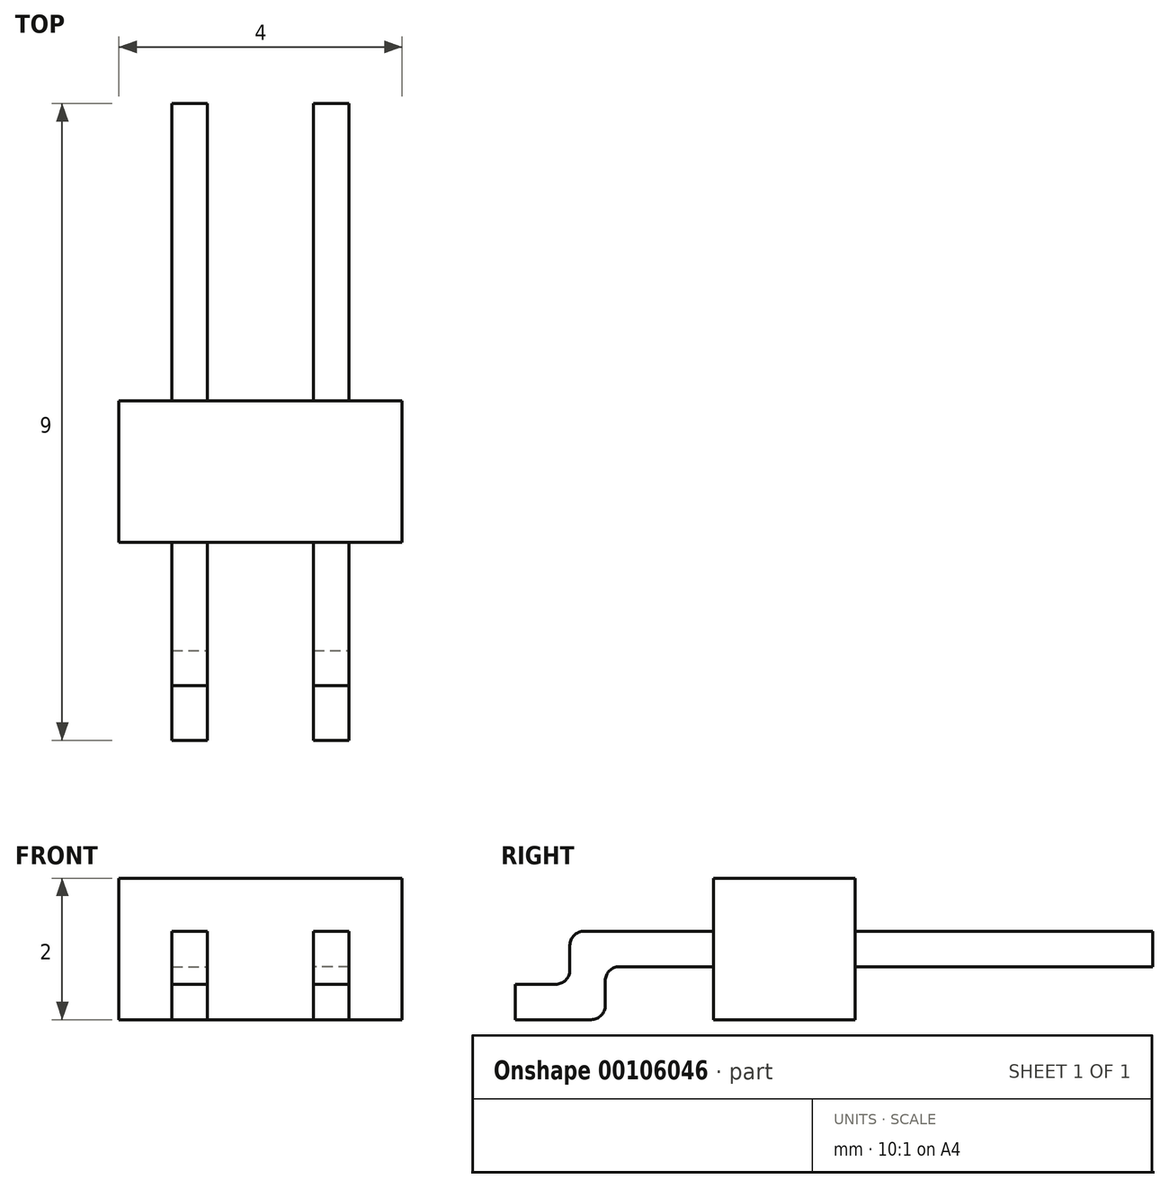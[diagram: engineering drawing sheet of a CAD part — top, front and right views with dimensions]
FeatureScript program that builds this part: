
annotation { "Feature Type Name" : "Feature", "Feature Type Description" : "" }
export const myFeature = defineFeature(function(context is Context, id is Id, definition is map)
    precondition{}
    {
        {
            var Q0;
            Q0=qCreatedBy(makeId("Top.planeOp"),FACE);
            var sketch = newSketch(context, id + "F0", { "sketchPlane" : qUnion([Q0])});
            skLineSegment(sketch, "E0.bottom", {"start": v(-2, 1) * mm, "end": v(2, 1) * mm});
            skLineSegment(sketch, "E0.top", {"start": v(-2, -1) * mm, "end": v(2, -1) * mm});
            skLineSegment(sketch, "E0.left", {"start": v(-2, 1) * mm, "end": v(-2, -1) * mm});
            skLineSegment(sketch, "E0.right", {"start": v(2, 1) * mm, "end": v(2, -1) * mm});
            skSolve(sketch);
        }
        {
            var Q0;
            Q0 = qSketchRegion(id + "F0", true);
            extrude(context, id + "F1", {"entities" : qUnion([Q0]), "depth" : 2 * mm});
        }
        {
            var Q0;
            Q0=makeQuery(id+"F1.opExtrude","SWEPT_FACE",FACE,{"disambiguationData":[OSD([sQuery(id+"F0.wireOp",EDGE,"E0.bottom")])]});
            var sketch = newSketch(context, id + "F2", { "sketchPlane" : qUnion([Q0])});
            skLineSegment(sketch, "E1.bottom", {"start": v(-1.25, 1.25) * mm, "end": v(-0.75, 1.25) * mm});
            skLineSegment(sketch, "E1.top", {"start": v(-1.25, 0.75) * mm, "end": v(-0.75, 0.75) * mm});
            skLineSegment(sketch, "E1.left", {"start": v(-1.25, 1.25) * mm, "end": v(-1.25, 0.75) * mm});
            skLineSegment(sketch, "E1.right", {"start": v(-0.75, 1.25) * mm, "end": v(-0.75, 0.75) * mm});
            skLineSegment(sketch, "E2.MirrorCS", {"start": v(0.75, 1.25) * mm, "end": v(0.75, 0.75) * mm});
            skLineSegment(sketch, "E3.MirrorCS", {"start": v(1.25, 1.25) * mm, "end": v(1.25, 0.75) * mm});
            skLineSegment(sketch, "E4.MirrorCS", {"start": v(1.25, 1.25) * mm, "end": v(0.75, 1.25) * mm});
            skLineSegment(sketch, "E5.MirrorCS", {"start": v(1.25, 0.75) * mm, "end": v(0.75, 0.75) * mm});
            skSolve(sketch);
        }
        {
            var Q0;
            Q0 = qSketchRegion(id + "F2", true);
            extrude(context, id + "F3", {"entities" : qUnion([Q0]), "depth" : 4.2 * mm});
        }
        {
            var Q0;
            Q0=makeQuery(id+"F3.opExtrude","SWEPT_FACE",FACE,{"disambiguationData":[OSD([sQuery(id+"F2.wireOp",EDGE,"E1.left")])]});
            var sketch = newSketch(context, id + "F4", { "sketchPlane" : qUnion([Q0])});
            skLineSegment(sketch, "E6.top", {"start": v(-1, 0.75) * mm, "end": v(-2.33, 0.75) * mm});
            skLineSegment(sketch, "E6.left", {"start": v(-1, 1.25) * mm, "end": v(-1, 0.75) * mm});
            skLineSegment(sketch, "E7.bottom", {"start": v(-3.8, 0) * mm, "end": v(-2.73, 0) * mm});
            skLineSegment(sketch, "E7.top", {"start": v(-3.8, 0.5) * mm, "end": v(-3.23, 0.5) * mm});
            skLineSegment(sketch, "E7.left", {"start": v(-3.8, 0) * mm, "end": v(-3.8, 0.5) * mm});
            skLineSegment(sketch, "E7.right", {"start": v(-2.53, 0.2) * mm, "end": v(-2.53, 0.6) * mm});
            skPoint(sketch, "E8.visualSharp", {"position": v(-2.53, 0) * mm});
            skArc(sketch, "E8.filletArc", {"start": v(-2.73, 0) * mm, "mid": v(-2.59, 0.06) * mm, "end": v(-2.53, 0.2) * mm});
            skLineSegment(sketch, "E9.bottom", {"start": v(-2.53, 0.2) * mm, "end": v(-3.13, 0.2) * mm});
            skLineSegment(sketch, "E9.top", {"start": v(-2.53, 1.25) * mm, "end": v(-2.83, 1.25) * mm});
            skLineSegment(sketch, "E9.left", {"start": v(-2.53, 0.2) * mm, "end": v(-2.53, 0.55) * mm});
            skLineSegment(sketch, "E9.right", {"start": v(-3.03, 0.7) * mm, "end": v(-3.03, 1.05) * mm});
            skArc(sketch, "E10.filletArc", {"start": v(-3.23, 0.5) * mm, "mid": v(-3.09, 0.56) * mm, "end": v(-3.03, 0.7) * mm});
            skPoint(sketch, "E11.visualSharp", {"position": v(-3.03, 1.25) * mm});
            skArc(sketch, "E11.filletArc", {"start": v(-2.83, 1.25) * mm, "mid": v(-2.97, 1.2) * mm, "end": v(-3.03, 1.05) * mm});
            skPoint(sketch, "E12.newPointA", {"position": v(-3.8, 0.75) * mm});
            skArc(sketch, "E12.filletArc", {"start": v(-2.33, 0.75) * mm, "mid": v(-2.47, 0.7) * mm, "end": v(-2.53, 0.55) * mm});
            skLineSegment(sketch, "E13", {"start": v(-2.53, 1.25) * mm, "end": v(-1, 1.25) * mm});
            skSolve(sketch);
        }
        {
            var Q0;
            Q0 = qSketchRegion(id + "F4", true);
            extrude(context, id + "F5", {"entities" : qUnion([Q0]), "oppositeDirection" : true, "depth" : 2.5 * mm});
        }
        {
            var Q0;
            Q0=makeQuery(id+"F5.opExtrude","SWEPT_FACE",FACE,{"disambiguationData":[OSD([sQuery(id+"F4.wireOp",EDGE,"E7.left")])]});
            var sketch = newSketch(context, id + "F6", { "sketchPlane" : qUnion([Q0])});
            skLineSegment(sketch, "E14.bottom", {"start": v(-0.75, 0) * mm, "end": v(0.75, 0) * mm});
            skLineSegment(sketch, "E14.top", {"start": v(-0.75, 1.44) * mm, "end": v(0.75, 1.44) * mm});
            skLineSegment(sketch, "E14.left", {"start": v(-0.75, 0) * mm, "end": v(-0.75, 1.44) * mm});
            skLineSegment(sketch, "E14.right", {"start": v(0.75, 0) * mm, "end": v(0.75, 1.44) * mm});
            skSolve(sketch);
        }
        {
            var Q0;
            Q0 = qSketchRegion(id + "F6", true);
            extrude(context, id + "F7", {"entities" : qUnion([Q0]), "operationType" : NewBodyOperationType.REMOVE, "oppositeDirection" : true, "depth" : 2.8 * mm});
        }
    });
